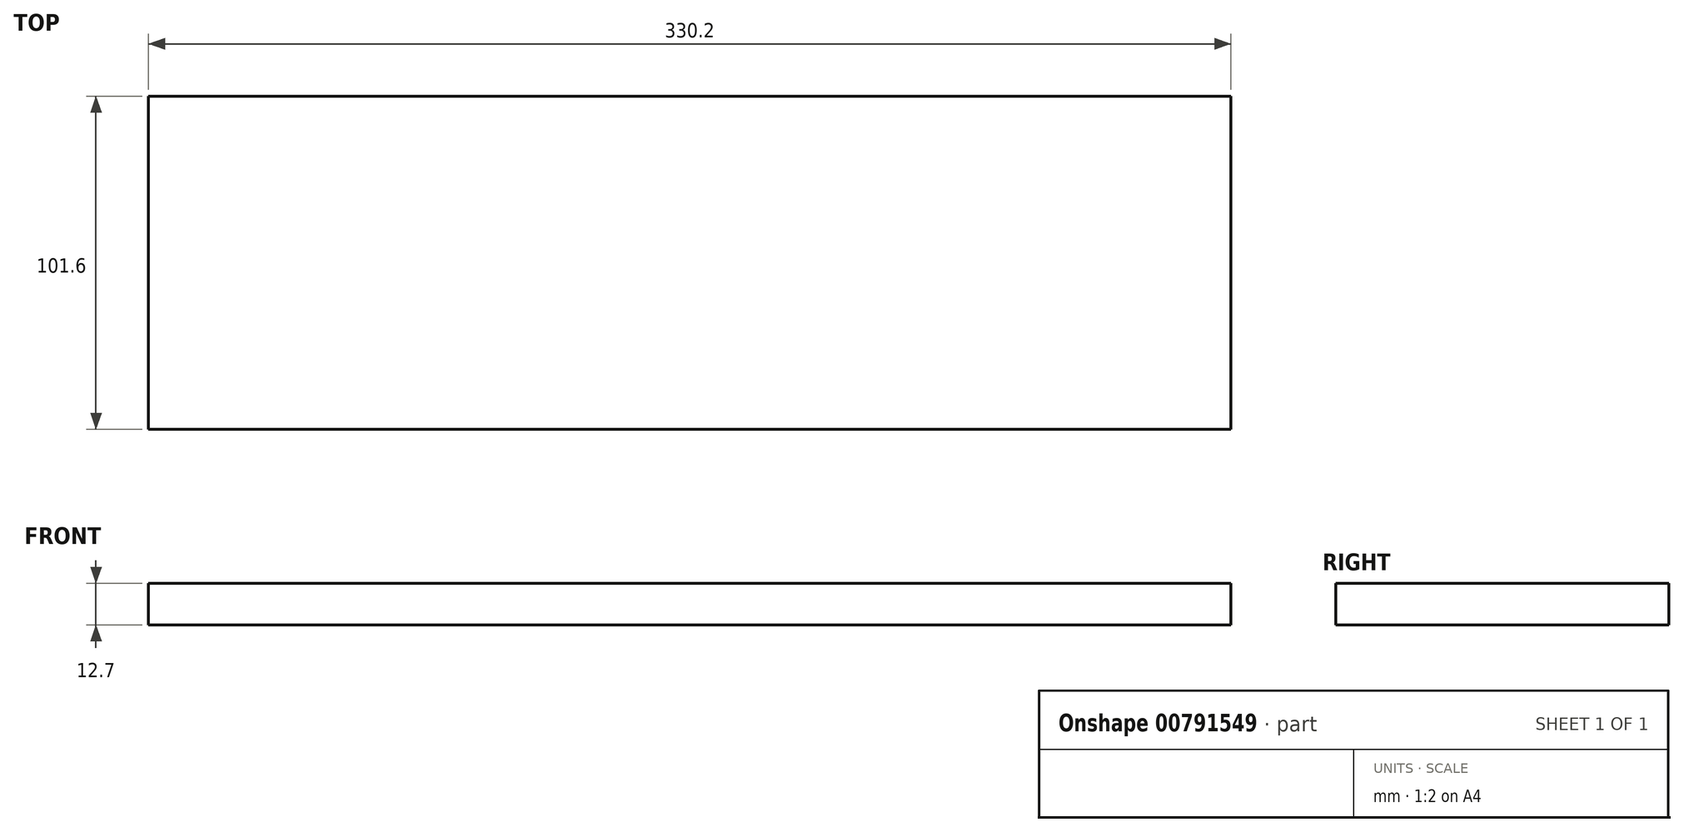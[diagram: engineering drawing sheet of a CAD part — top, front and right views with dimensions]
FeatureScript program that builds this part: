
annotation { "Feature Type Name" : "Feature", "Feature Type Description" : "" }
export const myFeature = defineFeature(function(context is Context, id is Id, definition is map)
    precondition{}
    {
        {
            var Q0;
            Q0=qCreatedBy(makeId("Front.planeOp"),FACE);
            var sketch = newSketch(context, id + "F0", { "sketchPlane" : qUnion([Q0])});
            skLineSegment(sketch, "E0.bottom", {"start": v(0, 0) * mm, "end": v(330.2, 0) * mm});
            skLineSegment(sketch, "E0.top", {"start": v(0, 12.7) * mm, "end": v(330.2, 12.7) * mm});
            skLineSegment(sketch, "E0.left", {"start": v(0, 0) * mm, "end": v(0, 12.7) * mm});
            skLineSegment(sketch, "E0.right", {"start": v(330.2, 0) * mm, "end": v(330.2, 12.7) * mm});
            skSolve(sketch);
        }
        {
            var Q0;
            Q0=makeQuery(id+"F0.imprint","IMPRINT",FACE,{"disambiguationData":[TD([[makeQuery(id+"F0.imprint","IMPRINT",EDGE,{"derivedFrom":sQuery(id+"F0.wireOp",EDGE,"E0.bottom")}),1.0]])]});
            extrude(context, id + "F1", {"entities" : qUnion([Q0]), "depth" : 101.6 * mm, "offsetDistance" : 25.4 * mm});
        }
    });
